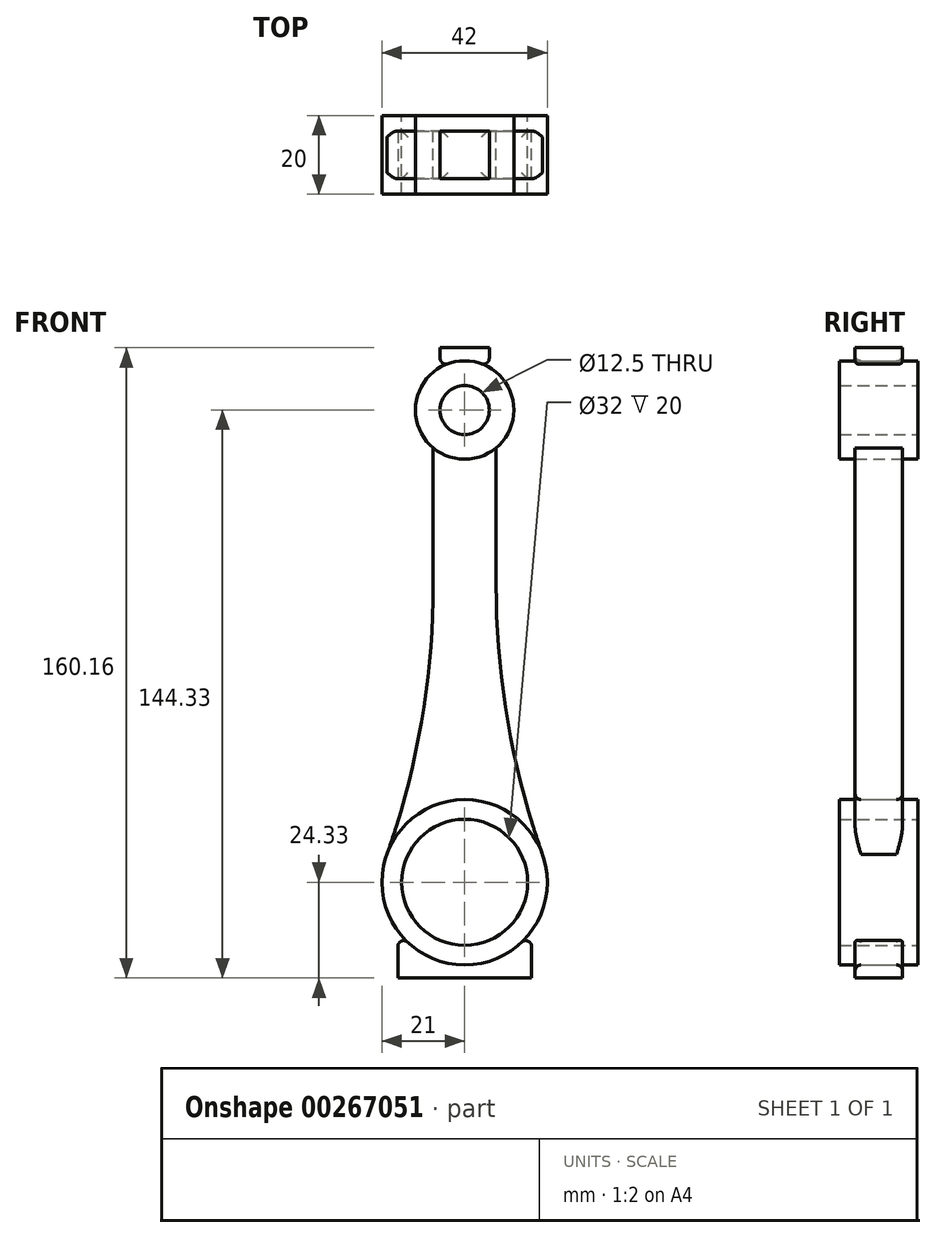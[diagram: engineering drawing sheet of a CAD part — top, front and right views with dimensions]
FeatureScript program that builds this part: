
annotation { "Feature Type Name" : "Feature", "Feature Type Description" : "" }
export const myFeature = defineFeature(function(context is Context, id is Id, definition is map)
    precondition{}
    {
        {
            var Q0;
            Q0=qCreatedBy(makeId("Front.planeOp"),FACE);
            var sketch = newSketch(context, id + "F0", { "sketchPlane" : qUnion([Q0])});
            skCircle(sketch, "E0", {"center": v(0, 0) * mm, "radius": 21 * mm});
            skCircle(sketch, "E1", {"center": v(0, 0) * mm, "radius": 16 * mm});
            skCircle(sketch, "E2", {"center": v(0, 120) * mm, "radius": 12.5 * mm});
            skCircle(sketch, "E3", {"center": v(0, 120) * mm, "radius": 6.25 * mm});
            skSolve(sketch);
        }
        {
            var Q0;
            Q0 = qSketchRegion(id + "F0", true);
            extrude(context, id + "F1", {"entities" : qUnion([Q0]), "endBound" : BoundingType.SYMMETRIC, "depth" : 20 * mm});
        }
        {
            var Q0;
            Q0=qCreatedBy(makeId("Front.planeOp"),FACE);
            var sketch = newSketch(context, id + "F2", { "sketchPlane" : qUnion([Q0])});
            skLineSegment(sketch, "E4", {"start": v(8, 110.4) * mm, "end": v(8, 75.4) * mm});
            skCircle(sketch, "E5.0", {"center": v(0, 120) * mm, "radius": 12.5 * mm});
            skCircle(sketch, "E6.0", {"center": v(0, 0) * mm, "radius": 21 * mm});
            skArc(sketch, "E7", {"start": v(8, 75.4) * mm, "mid": v(10.97, 40.7) * mm, "end": v(19.79, 7.03) * mm});
            skArc(sketch, "E8.MirrorCS", {"start": v(-8, 75.4) * mm, "mid": v(-10.97, 40.7) * mm, "end": v(-19.79, 7.03) * mm});
            skLineSegment(sketch, "E9.MirrorCS", {"start": v(-8, 110.4) * mm, "end": v(-8, 75.4) * mm});
            skSolve(sketch);
        }
        {
            var Q0;
            {var subQ4=sQuery(id+"F2.wireOp",EDGE,"E4");Q0=makeQuery(id+"F2.imprint","IMPRINT",FACE,{"disambiguationData":[TD([[makeQuery(id+"F2.imprint","IMPRINT",EDGE,{"derivedFrom":subQ4}),-1.0]])]});}
            extrude(context, id + "F3", {"entities" : qUnion([Q0]), "endBound" : BoundingType.SYMMETRIC, "depth" : 12 * mm});
        }
        {
            var Q0;
            Q0=qCreatedBy(makeId("Front.planeOp"),FACE);
            var sketch = newSketch(context, id + "F4", { "sketchPlane" : qUnion([Q0])});
            skArc(sketch, "E10.0", {"start": v(6.25, 130.83) * mm, "mid": v(0, 132.5) * mm, "end": v(-6.25, 130.83) * mm});
            skLineSegment(sketch, "E11", {"start": v(-6.25, 130.83) * mm, "end": v(-6.25, 135.83) * mm});
            skLineSegment(sketch, "E12.MirrorCS", {"start": v(6.25, 130.83) * mm, "end": v(6.25, 135.83) * mm});
            skLineSegment(sketch, "E13", {"start": v(-6.25, 135.83) * mm, "end": v(6.25, 135.83) * mm});
            skArc(sketch, "E14.0", {"start": v(-17, -12.33) * mm, "mid": v(0, -21) * mm, "end": v(17, -12.33) * mm});
            skLineSegment(sketch, "E15", {"start": v(-17, -12.33) * mm, "end": v(-17, -24.33) * mm});
            skLineSegment(sketch, "E16.MirrorCS", {"start": v(17, -12.33) * mm, "end": v(17, -24.33) * mm});
            skLineSegment(sketch, "E17", {"start": v(-17, -24.33) * mm, "end": v(17, -24.33) * mm});
            skSolve(sketch);
        }
        {
            var Q0;
            Q0 = qSketchRegion(id + "F4", true);
            extrude(context, id + "F5", {"entities" : qUnion([Q0]), "endBound" : BoundingType.SYMMETRIC, "depth" : 12 * mm});
        }
        {
            var Q0;
            Q0=makeQuery(id+"F5.opExtrude","CAP_EDGE",EDGE,{"disambiguationData":[OSD([sQuery(id+"F4.wireOp",EDGE,"E10.0")])],"isStart":false});
            var Q1;
            Q1=makeQuery(id+"F5.opExtrude","SWEPT_EDGE",EDGE,{"disambiguationData":[OSD([sQuery(id+"F4.wireOp",EDGE,"E10.0"),sQuery(id+"F4.wireOp",EDGE,"E12.MirrorCS")])]});
            var Q2;
            Q2=makeQuery(id+"F5.opExtrude","CAP_EDGE",EDGE,{"disambiguationData":[OSD([sQuery(id+"F4.wireOp",EDGE,"E10.0")])],"isStart":true});
            var Q3;
            Q3=makeQuery(id+"F5.opExtrude","SWEPT_EDGE",EDGE,{"disambiguationData":[OSD([sQuery(id+"F4.wireOp",EDGE,"E10.0"),sQuery(id+"F4.wireOp",EDGE,"E11")])]});
            var Q4;
            Q4=makeQuery(id+"F3.opExtrude","CAP_EDGE",EDGE,{"disambiguationData":[OSD([sQuery(id+"F2.wireOp",EDGE,"E6.0")])],"isStart":false});
            var Q5;
            Q5=makeQuery(id+"F3.opExtrude","CAP_EDGE",EDGE,{"disambiguationData":[OSD([sQuery(id+"F2.wireOp",EDGE,"E6.0")])],"isStart":true});
            var Q6;
            Q6=makeQuery(id+"F5.opExtrude","SWEPT_EDGE",EDGE,{"disambiguationData":[OSD([sQuery(id+"F4.wireOp",EDGE,"E14.0"),sQuery(id+"F4.wireOp",EDGE,"E16.MirrorCS")])]});
            var Q7;
            Q7=makeQuery(id+"F5.opExtrude","CAP_EDGE",EDGE,{"disambiguationData":[OSD([sQuery(id+"F4.wireOp",EDGE,"E14.0")])],"isStart":false});
            var Q8;
            Q8=makeQuery(id+"F5.opExtrude","CAP_EDGE",EDGE,{"disambiguationData":[OSD([sQuery(id+"F4.wireOp",EDGE,"E14.0")])],"isStart":true});
            var Q9;
            Q9=makeQuery(id+"F5.opExtrude","SWEPT_EDGE",EDGE,{"disambiguationData":[OSD([sQuery(id+"F4.wireOp",EDGE,"E14.0"),sQuery(id+"F4.wireOp",EDGE,"E15")])]});
            fillet(context, id + "F6", {"entities" : qUnion([Q0, Q1, Q2, Q3, Q4, Q5, Q6, Q7, Q8, Q9]), "radius" : 1.5 * mm, "tangentPropagation" : true, "allowEdgeOverflow" : false});
        }
    });
